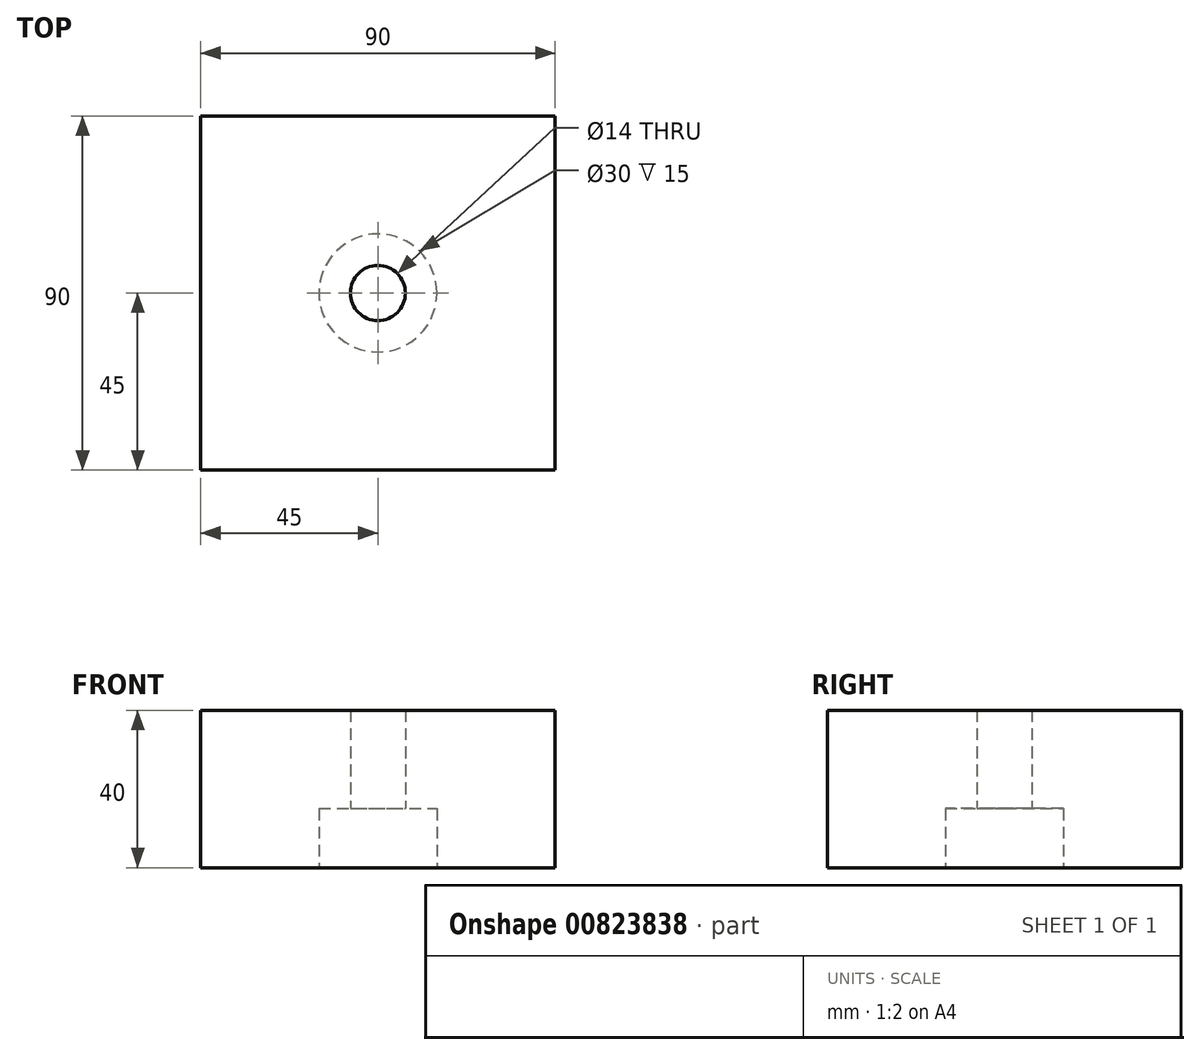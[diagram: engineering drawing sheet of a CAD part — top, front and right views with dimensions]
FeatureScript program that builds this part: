
annotation { "Feature Type Name" : "Feature", "Feature Type Description" : "" }
export const myFeature = defineFeature(function(context is Context, id is Id, definition is map)
    precondition{}
    {
        {
            var Q0;
            Q0=qCreatedBy(makeId("Top.planeOp"),FACE);
            var sketch = newSketch(context, id + "F0", { "sketchPlane" : qUnion([Q0])});
            skLineSegment(sketch, "E0.bottom", {"start": v(0, 0) * mm, "end": v(90, 0) * mm});
            skLineSegment(sketch, "E0.top", {"start": v(0, 90) * mm, "end": v(90, 90) * mm});
            skLineSegment(sketch, "E0.left", {"start": v(0, 0) * mm, "end": v(0, 90) * mm});
            skLineSegment(sketch, "E0.right", {"start": v(90, 0) * mm, "end": v(90, 90) * mm});
            skCircle(sketch, "E1", {"center": v(45, 45) * mm, "radius": 7 * mm});
            skSolve(sketch);
        }
        {
            var Q0;
            Q0=makeQuery(id+"F0.imprint","IMPRINT",FACE,{"disambiguationData":[TD([[makeQuery(id+"F0.imprint","IMPRINT",EDGE,{"derivedFrom":sQuery(id+"F0.wireOp",EDGE,"E0.bottom")}),1.0]])]});
            extrude(context, id + "F1", {"entities" : qUnion([Q0]), "depth" : 40 * mm, "offsetDistance" : 25 * mm});
        }
        {
            var Q0;
            Q0=makeQuery(id+"F1.opExtrude","CAP_FACE",FACE,{"disambiguationData":[OSD([sQuery(id+"F0.wireOp",EDGE,"E0.bottom"),sQuery(id+"F0.wireOp",EDGE,"E0.top"),sQuery(id+"F0.wireOp",EDGE,"E0.left"),sQuery(id+"F0.wireOp",EDGE,"E0.right"),sQuery(id+"F0.wireOp",EDGE,"E1")])],"isStart":true});
            var sketch = newSketch(context, id + "F2", { "sketchPlane" : qUnion([Q0])});
            skCircle(sketch, "E2", {"center": v(45, -45) * mm, "radius": 15 * mm});
            skSolve(sketch);
        }
        {
            var Q0;
            Q0 = qSketchRegion(id + "F2", true);
            extrude(context, id + "F3", {"entities" : qUnion([Q0]), "operationType" : NewBodyOperationType.REMOVE, "oppositeDirection" : true, "depth" : 15 * mm, "offsetDistance" : 25 * mm});
        }
    });
